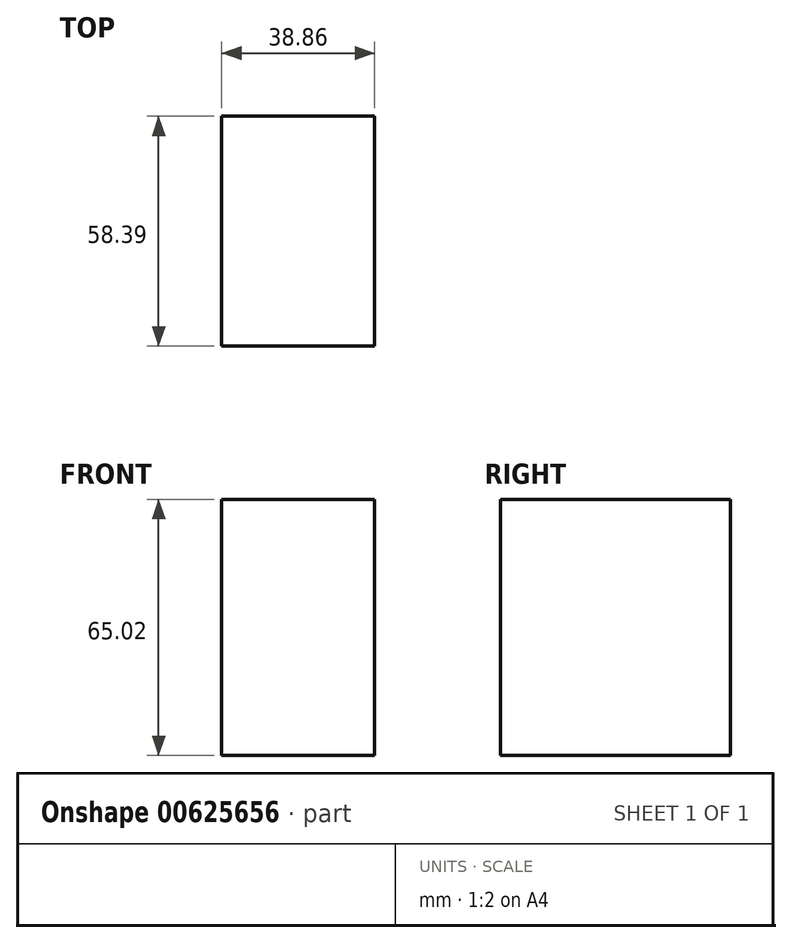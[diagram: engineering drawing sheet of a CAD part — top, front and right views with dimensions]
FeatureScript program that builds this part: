
annotation { "Feature Type Name" : "Feature", "Feature Type Description" : "" }
export const myFeature = defineFeature(function(context is Context, id is Id, definition is map)
    precondition{}
    {
        {
            var Q0;
            Q0=qCreatedBy(makeId("Top.planeOp"),FACE);
            var sketch = newSketch(context, id + "F0", { "sketchPlane" : qUnion([Q0])});
            skLineSegment(sketch, "E0.bottom", {"start": v(0, 0) * mm, "end": v(-38.86, 0) * mm});
            skLineSegment(sketch, "E0.top", {"start": v(0, 58.39) * mm, "end": v(-38.86, 58.39) * mm});
            skLineSegment(sketch, "E0.left", {"start": v(0, 0) * mm, "end": v(0, 58.39) * mm});
            skLineSegment(sketch, "E0.right", {"start": v(-38.86, 0) * mm, "end": v(-38.86, 58.39) * mm});
            skSolve(sketch);
        }
        {
            var Q0;
            Q0=makeQuery(id+"F0.imprint","IMPRINT",FACE,{"disambiguationData":[TD([[makeQuery(id+"F0.imprint","IMPRINT",EDGE,{"derivedFrom":sQuery(id+"F0.wireOp",EDGE,"E0.bottom")}),-1.0]])]});
            extrude(context, id + "F1", {"entities" : qUnion([Q0]), "oppositeDirection" : true, "depth" : 65.02 * mm, "offsetDistance" : 25.4 * mm});
        }
    });
